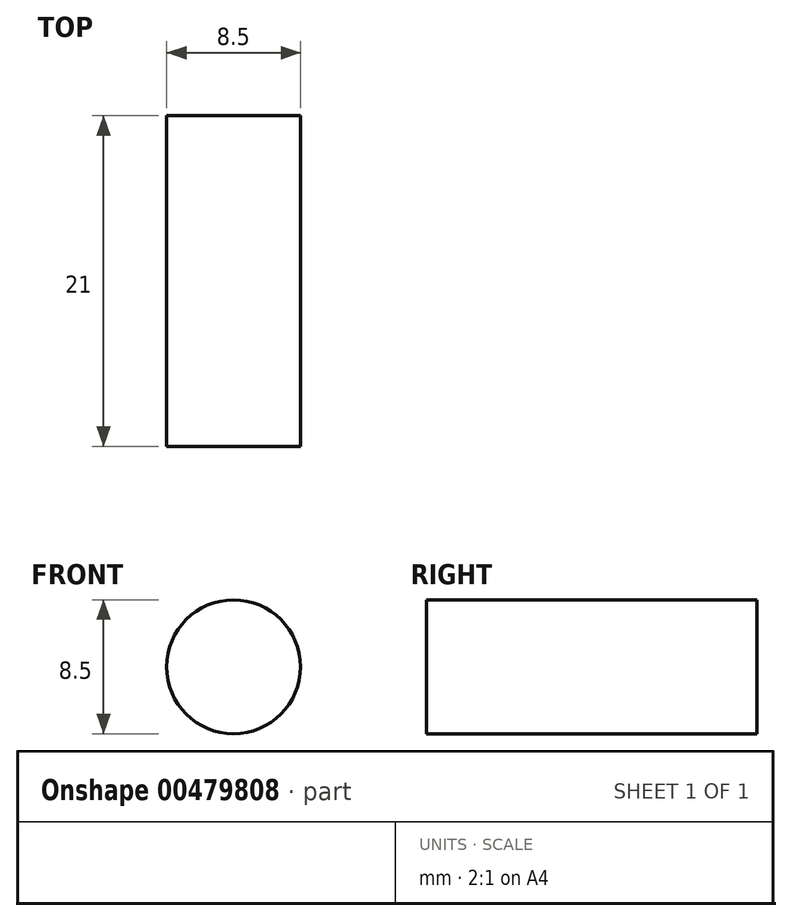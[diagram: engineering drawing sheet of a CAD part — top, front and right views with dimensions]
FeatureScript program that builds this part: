
annotation { "Feature Type Name" : "Feature", "Feature Type Description" : "" }
export const myFeature = defineFeature(function(context is Context, id is Id, definition is map)
    precondition{}
    {
        {
            var Q0;
            Q0=qCreatedBy(makeId("Front.planeOp"),FACE);
            var sketch = newSketch(context, id + "F0", { "sketchPlane" : qUnion([Q0])});
            skCircle(sketch, "E0", {"center": v(-108.07, 3.02) * mm, "radius": 4.25 * mm});
            skSolve(sketch);
        }
        {
            var Q0;
            Q0=makeQuery(id+"F0.imprint","IMPRINT",FACE,{"disambiguationData":[TD([[makeQuery(id+"F0.imprint","IMPRINT",EDGE,{"derivedFrom":sQuery(id+"F0.wireOp",EDGE,"E0")}),1.0]])]});
            extrude(context, id + "F1", {"entities" : qUnion([Q0]), "depth" : 21 * mm});
        }
    });
